# Revit family: Trane_TVR_Indoor_Ceiling & Floor_4TVX0027(30)EF000AA(2nd DC)
name_source: partatom
category: Equipamento mecânico
units: mm (PartAtom-declared; Revit-internal decimal feet)

## family parameters
Com base no plano de trabalho = Não
Compartilhado = Não
Corte com vazios quando carregada = Não
Cota do conector redondo = Utilizar diâmetro
Número OmniClass = 23.75.00.00
Ponto de cálculo do ambiente = Não
Sempre na vertical = Sim
Tipo de parte = Normal
Título OmniClass = Climate Control (HVAC)

## types (2) — shared parameters
Air  Flow = 1200/1100/1000/900/840/780/700 m3/h
Condensation = air
Cooling Power Input = 130 W
Depth = 660
Descrição = High efficiency air cooled
Fabricante = Trane
Gas = R410a
Gas pipe = 15.9  [stored 0.0521654 ft]
Heating Power Input = 130 W
Height = 203  [stored 0.66601 ft]
Installation = Indoor installation
Liquid pipe = 9.53
MCA (Minimum Circuit Amps) = 1 A
MFA (Maximum Fuse Amps) = 15 A
Machine material = Galvanized Steel
Net Weight = 35.00 kg
Panel color = S1004
Power supply = 220-240V ~50/60Hz
Series = TVR ULTRA
URL = https://www.trane.com
Width = 1280  [stored 4.19948 ft]

## per-type parameters (varying)
| type | Cooling Capacity | Heating Capacity |
| 4TVX0027EF000AA | 8 kW | 9 kW |
| 4TVX0030EF000AA | 9 kW | 10 kW |

note: column(s) folded — value = type name in every type: Modelo

note: [stored X ft] marks values corroborated as IEEE doubles in the binary element streams (Revit-internal decimal feet)
